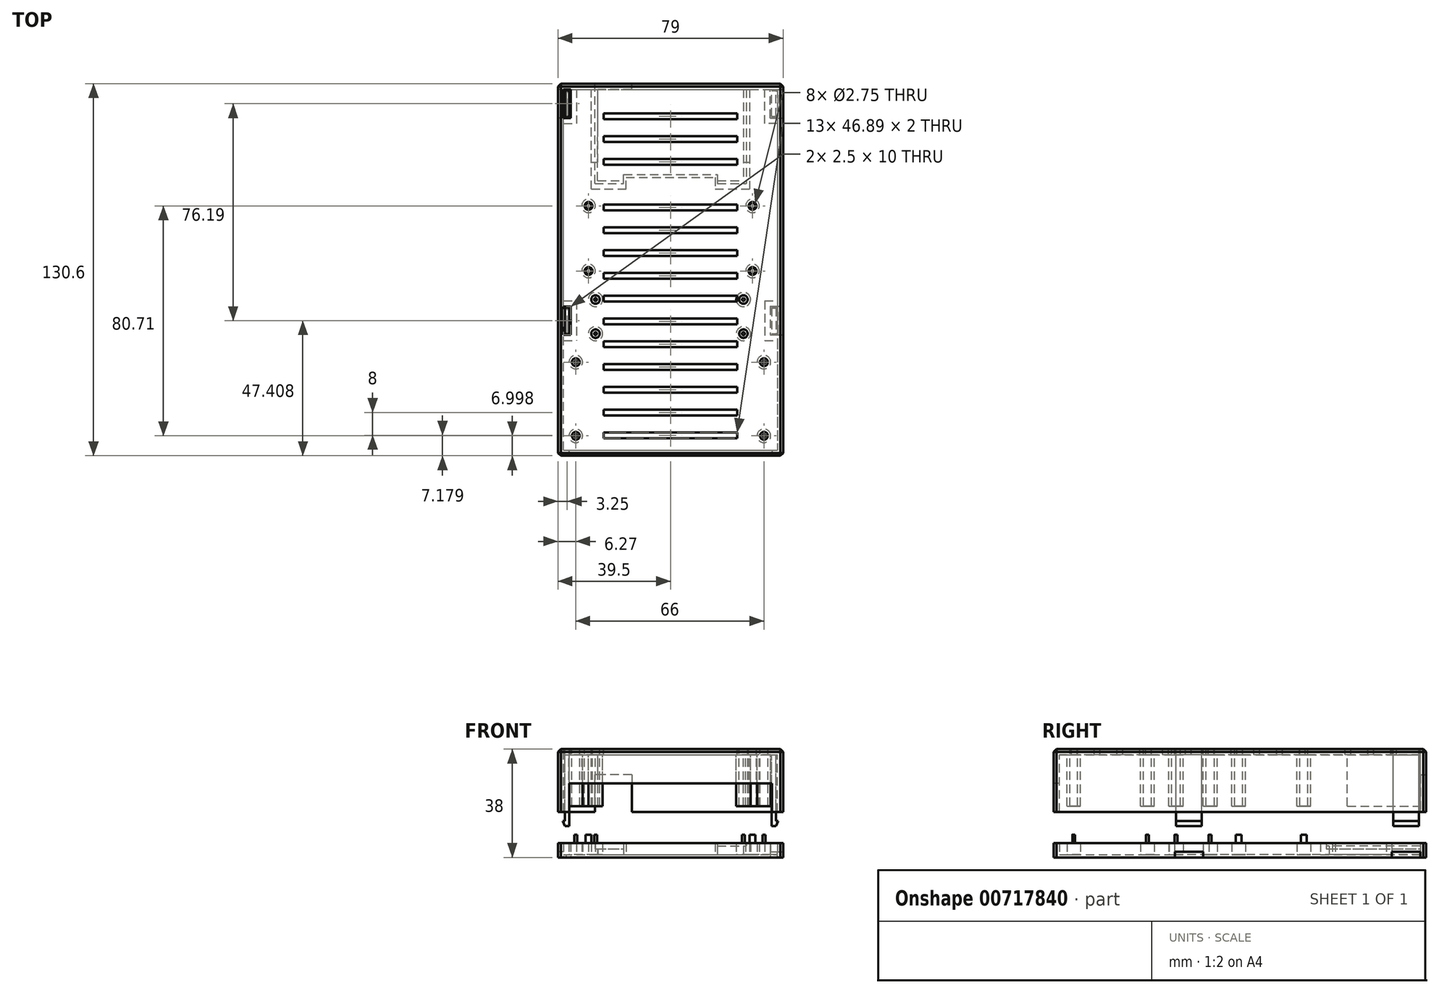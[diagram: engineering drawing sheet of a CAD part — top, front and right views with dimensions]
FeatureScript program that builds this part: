
annotation { "Feature Type Name" : "Feature", "Feature Type Description" : "" }
export const myFeature = defineFeature(function(context is Context, id is Id, definition is map)
    precondition{}
    {
        {
            var Q0;
            Q0=qCreatedBy(makeId("Top.planeOp"),FACE);
            var sketch = newSketch(context, id + "F0", { "sketchPlane" : qUnion([Q0])});
            skLineSegment(sketch, "E0", {"start": v(-75, 58.75) * mm, "end": v(0, 58.75) * mm});
            skLineSegment(sketch, "E1", {"start": v(0, 58.75) * mm, "end": v(0, -67.85) * mm});
            skLineSegment(sketch, "E2", {"start": v(-75, -67.85) * mm, "end": v(-75, 58.75) * mm});
            skCircle(sketch, "E3", {"center": v(-8.73, -5) * mm, "radius": 1 * mm});
            skCircle(sketch, "E4", {"center": v(-66.27, -5) * mm, "radius": 1 * mm});
            skCircle(sketch, "E5", {"center": v(-8.73, 17.86) * mm, "radius": 1 * mm});
            skCircle(sketch, "E6", {"center": v(-66.27, 17.86) * mm, "radius": 1 * mm});
            skLineSegment(sketch, "E7", {"start": v(-75, 17.86) * mm, "end": v(-66.27, 17.86) * mm, "construction": true});
            skLineSegment(sketch, "E8", {"start": v(-8.73, 17.86) * mm, "end": v(0, 17.86) * mm, "construction": true});
            skCircle(sketch, "E9", {"center": v(-66.27, 17.86) * mm, "radius": 2.38 * mm});
            skCircle(sketch, "E10", {"center": v(-66.27, -5) * mm, "radius": 2.38 * mm});
            skCircle(sketch, "E11", {"center": v(-8.73, -5) * mm, "radius": 2.38 * mm});
            skCircle(sketch, "E12", {"center": v(-8.73, 17.86) * mm, "radius": 2.38 * mm});
            skLineSegment(sketch, "E13", {"start": v(-10.95, 58.75) * mm, "end": v(-10.96, 25.75) * mm});
            skLineSegment(sketch, "E14", {"start": v(-64.06, 25.75) * mm, "end": v(-64.05, 58.75) * mm});
            skLineSegment(sketch, "E15", {"start": v(-64.06, 25.75) * mm, "end": v(-53.94, 25.75) * mm});
            skLineSegment(sketch, "E16", {"start": v(-53.94, 25.75) * mm, "end": v(-53.94, 28.86) * mm});
            skLineSegment(sketch, "E17", {"start": v(-53.94, 28.86) * mm, "end": v(-21.08, 28.86) * mm});
            skLineSegment(sketch, "E18", {"start": v(-21.08, 28.86) * mm, "end": v(-21.08, 25.75) * mm});
            skLineSegment(sketch, "E19", {"start": v(-21.08, 25.75) * mm, "end": v(-10.96, 25.75) * mm});
            skLineSegment(sketch, "E20", {"start": v(-75, 47.35) * mm, "end": v(-64.05, 47.35) * mm, "construction": true});
            skLineSegment(sketch, "E21", {"start": v(-10.95, 47.22) * mm, "end": v(0, 47.22) * mm, "construction": true});
            skCircle(sketch, "E22", {"center": v(-11.92, -27) * mm, "radius": 0.5 * mm});
            skCircle(sketch, "E23", {"center": v(-11.92, -15) * mm, "radius": 0.5 * mm});
            skCircle(sketch, "E24", {"center": v(-63.8, -15) * mm, "radius": 0.5 * mm});
            skCircle(sketch, "E25", {"center": v(-63.8, -27) * mm, "radius": 0.5 * mm});
            skCircle(sketch, "E26", {"center": v(-63.8, -27) * mm, "radius": 2.5 * mm});
            skCircle(sketch, "E27", {"center": v(-63.8, -15) * mm, "radius": 2.5 * mm});
            skLineSegment(sketch, "E28.0", {"start": v(-65.26, 23.75) * mm, "end": v(-65.26, 58.75) * mm});
            skLineSegment(sketch, "E28.1", {"start": v(-65.26, 23.75) * mm, "end": v(-53.14, 23.75) * mm});
            skLineSegment(sketch, "E28.3", {"start": v(-53.14, 23.75) * mm, "end": v(-53.14, 27.86) * mm});
            skLineSegment(sketch, "E28.4", {"start": v(-9.74, 58.75) * mm, "end": v(-9.74, 23.75) * mm});
            skLineSegment(sketch, "E28.5", {"start": v(-21.86, 23.75) * mm, "end": v(-9.74, 23.75) * mm});
            skLineSegment(sketch, "E28.6", {"start": v(-21.86, 27.86) * mm, "end": v(-21.86, 23.75) * mm});
            skLineSegment(sketch, "E28.7", {"start": v(-53.14, 27.86) * mm, "end": v(-21.86, 27.86) * mm});
            skLineSegment(sketch, "E29.1", {"start": v(-63.06, 26.75) * mm, "end": v(-53.94, 26.75) * mm});
            skLineSegment(sketch, "E29.2", {"start": v(-63.06, 26.75) * mm, "end": v(-63.05, 58.75) * mm});
            skLineSegment(sketch, "E30.0", {"start": v(-11.95, 58.75) * mm, "end": v(-11.96, 26.75) * mm});
            skLineSegment(sketch, "E30.1", {"start": v(-21.08, 26.75) * mm, "end": v(-11.96, 26.75) * mm});
            skLineSegment(sketch, "E31", {"start": v(-75, -67.85) * mm, "end": v(0, -67.85) * mm});
            skCircle(sketch, "E32", {"center": v(-4.73, -62.85) * mm, "radius": 0.5 * mm});
            skCircle(sketch, "E33", {"center": v(-70.73, -62.85) * mm, "radius": 0.5 * mm});
            skCircle(sketch, "E34", {"center": v(-4.73, -37) * mm, "radius": 0.5 * mm});
            skCircle(sketch, "E35", {"center": v(-70.73, -37) * mm, "radius": 0.5 * mm});
            skCircle(sketch, "E36", {"center": v(-70.73, -37) * mm, "radius": 2.38 * mm});
            skCircle(sketch, "E37", {"center": v(-70.73, -62.85) * mm, "radius": 2.38 * mm});
            skCircle(sketch, "E38", {"center": v(-4.73, -62.85) * mm, "radius": 2.38 * mm});
            skCircle(sketch, "E39", {"center": v(-4.73, -37) * mm, "radius": 2.38 * mm});
            skLineSegment(sketch, "E40", {"start": v(-70.73, -37) * mm, "end": v(-70.73, -27) * mm, "construction": true});
            skLineSegment(sketch, "E41", {"start": v(-4.73, -37) * mm, "end": v(0, -37) * mm, "construction": true});
            skLineSegment(sketch, "E42", {"start": v(-70.73, -37) * mm, "end": v(-75.46, -37) * mm, "construction": true});
            skCircle(sketch, "E43", {"center": v(-11.92, -15) * mm, "radius": 2.5 * mm});
            skCircle(sketch, "E44", {"center": v(-11.92, -27) * mm, "radius": 2.5 * mm});
            skLineSegment(sketch, "E45", {"start": v(-70.73, -62.85) * mm, "end": v(-4.73, -62.85) * mm, "construction": true});
            skLineSegment(sketch, "E46", {"start": v(-4.73, -37) * mm, "end": v(-4.73, -62.85) * mm, "construction": true});
            skLineSegment(sketch, "E47", {"start": v(-66.27, 17.86) * mm, "end": v(-8.73, 17.86) * mm, "construction": true});
            skLineSegment(sketch, "E48", {"start": v(-66.27, 17.86) * mm, "end": v(-66.27, -5) * mm, "construction": true});
            skLineSegment(sketch, "E49", {"start": v(-66.27, -5) * mm, "end": v(-8.73, -5) * mm, "construction": true});
            skLineSegment(sketch, "E50", {"start": v(-8.73, -5) * mm, "end": v(-8.73, 17.86) * mm, "construction": true});
            skLineSegment(sketch, "E51", {"start": v(-70.73, -37) * mm, "end": v(-70.73, -62.85) * mm, "construction": true});
            skLineSegment(sketch, "E52", {"start": v(-70.73, -37) * mm, "end": v(-4.73, -37) * mm, "construction": true});
            skLineSegment(sketch, "E53", {"start": v(-63.8, -15) * mm, "end": v(-11.92, -15) * mm, "construction": true});
            skLineSegment(sketch, "E54", {"start": v(-11.93, -15) * mm, "end": v(-11.93, -27) * mm, "construction": true});
            skLineSegment(sketch, "E55", {"start": v(-11.92, -27) * mm, "end": v(-63.8, -27) * mm, "construction": true});
            skLineSegment(sketch, "E56", {"start": v(-63.8, -27) * mm, "end": v(-63.8, -15) * mm, "construction": true});
            skLineSegment(sketch, "E57", {"start": v(-11.92, -15) * mm, "end": v(0, -15) * mm, "construction": true});
            skLineSegment(sketch, "E58", {"start": v(-63.8, -27) * mm, "end": v(-75, -27) * mm, "construction": true});
            skLineSegment(sketch, "E59", {"start": v(-34.3, -27) * mm, "end": v(-34.3, -37) * mm, "construction": true});
            skLineSegment(sketch, "E60", {"start": v(-45.46, 27.86) * mm, "end": v(-45.46, 17.86) * mm});
            skPoint(sketch, "E61", {"position": v(-37.5, 17.86) * mm});
            skLineSegment(sketch, "E62", {"start": v(-8.73, -5) * mm, "end": v(0, -5) * mm, "construction": true});
            skLineSegment(sketch, "E63", {"start": v(-70.73, -62.85) * mm, "end": v(-70.73, -67.85) * mm, "construction": true});
            skLineSegment(sketch, "E64.0", {"start": v(-77, -69.85) * mm, "end": v(-77, 60.75) * mm});
            skLineSegment(sketch, "E64.1", {"start": v(-77, -69.85) * mm, "end": v(2, -69.85) * mm});
            skLineSegment(sketch, "E64.2", {"start": v(2, 60.75) * mm, "end": v(2, -69.85) * mm});
            skLineSegment(sketch, "E64.3", {"start": v(-77, 60.75) * mm, "end": v(2, 60.75) * mm});
            skLineSegment(sketch, "E65.bottom", {"start": v(-77, -15.44) * mm, "end": v(-70.5, -15.44) * mm});
            skLineSegment(sketch, "E65.top", {"start": v(-77, -29.44) * mm, "end": v(-70.5, -29.44) * mm});
            skLineSegment(sketch, "E65.left", {"start": v(-77, -15.44) * mm, "end": v(-77, -29.44) * mm});
            skLineSegment(sketch, "E65.right", {"start": v(-70.5, -15.44) * mm, "end": v(-70.5, -29.44) * mm});
            skLineSegment(sketch, "E66.0", {"start": v(-75, -17.44) * mm, "end": v(-72.5, -17.44) * mm});
            skLineSegment(sketch, "E66.1", {"start": v(-75, -17.44) * mm, "end": v(-75, -27.44) * mm});
            skLineSegment(sketch, "E66.2", {"start": v(-75, -27.44) * mm, "end": v(-72.5, -27.44) * mm});
            skLineSegment(sketch, "E66.3", {"start": v(-72.5, -17.44) * mm, "end": v(-72.5, -27.44) * mm});
            skLineSegment(sketch, "E67.bottom", {"start": v(-4.5, -15.44) * mm, "end": v(2, -15.44) * mm});
            skLineSegment(sketch, "E67.top", {"start": v(-4.5, -29.44) * mm, "end": v(2, -29.44) * mm});
            skLineSegment(sketch, "E67.left", {"start": v(-4.5, -15.44) * mm, "end": v(-4.5, -29.44) * mm});
            skLineSegment(sketch, "E67.right", {"start": v(2, -15.44) * mm, "end": v(2, -29.44) * mm});
            skLineSegment(sketch, "E68.0", {"start": v(-2.5, -17.44) * mm, "end": v(0, -17.44) * mm});
            skLineSegment(sketch, "E68.1", {"start": v(-2.5, -17.44) * mm, "end": v(-2.5, -27.44) * mm});
            skLineSegment(sketch, "E68.2", {"start": v(-2.5, -27.44) * mm, "end": v(0, -27.44) * mm});
            skLineSegment(sketch, "E68.3", {"start": v(0, -17.44) * mm, "end": v(0, -27.44) * mm});
            skLineSegment(sketch, "E69.bottom", {"start": v(-75, 58.75) * mm, "end": v(-72.5, 58.75) * mm});
            skLineSegment(sketch, "E69.top", {"start": v(-75, 48.75) * mm, "end": v(-72.5, 48.75) * mm});
            skLineSegment(sketch, "E69.left", {"start": v(-75, 58.75) * mm, "end": v(-75, 48.75) * mm});
            skLineSegment(sketch, "E69.right", {"start": v(-72.5, 58.75) * mm, "end": v(-72.5, 48.75) * mm});
            skLineSegment(sketch, "E70", {"start": v(0, 48.75) * mm, "end": v(-2.5, 48.75) * mm});
            skLineSegment(sketch, "E71", {"start": v(-2.5, 48.75) * mm, "end": v(-2.5, 58.75) * mm});
            skLineSegment(sketch, "E72.0", {"start": v(-4.5, 46.75) * mm, "end": v(-4.5, 58.75) * mm});
            skLineSegment(sketch, "E72.1", {"start": v(0, 46.75) * mm, "end": v(-4.5, 46.75) * mm});
            skLineSegment(sketch, "E73.0", {"start": v(-70.5, 58.75) * mm, "end": v(-70.5, 46.75) * mm});
            skLineSegment(sketch, "E73.1", {"start": v(-75, 46.75) * mm, "end": v(-70.5, 46.75) * mm});
            skSolve(sketch);
        }
        {
            var Q0;
            {var subQ10=sQuery(id+"F0.wireOp",EDGE,"E13");Q0=makeQuery(id+"F0.imprint","IMPRINT",FACE,{"disambiguationData":[TD([[makeQuery(id+"F0.imprint","IMPRINT",EDGE,{"derivedFrom":subQ10}),1.0]])]});}
            var Q1;
            Q1=sQuery(id+"F0.wireOp",EDGE,"E15");
            var Q2;
            Q2=sQuery(id+"F0.wireOp",EDGE,"E16");
            var Q3;
            Q3=sQuery(id+"F0.wireOp",EDGE,"E17");
            var Q4;
            Q4=sQuery(id+"F0.wireOp",EDGE,"E28.7");
            var Q5;
            Q5=sQuery(id+"F0.wireOp",EDGE,"E28.3");
            var Q6;
            Q6=sQuery(id+"F0.wireOp",EDGE,"E28.1");
            var Q7;
            Q7=sQuery(id+"F0.wireOp",EDGE,"E28.0");
            var Q8;
            Q8=sQuery(id+"F0.wireOp",EDGE,"E14");
            var Q9;
            Q9=sQuery(id+"F0.wireOp",EDGE,"E28.2");
            var Q10;
            Q10=sQuery(id+"F0.wireOp",EDGE,"XvR5vRtn-6RYL-8VlD-djdF-WygFPbgBNpBE");
            var Q11;
            Q11=sQuery(id+"F0.wireOp",EDGE,"E28.4");
            var Q12;
            Q12=sQuery(id+"F0.wireOp",EDGE,"E13");
            var Q13;
            Q13=sQuery(id+"F0.wireOp",EDGE,"E19");
            var Q14;
            Q14=sQuery(id+"F0.wireOp",EDGE,"E28.5");
            var Q15;
            Q15=sQuery(id+"F0.wireOp",EDGE,"E18");
            var Q16;
            Q16=sQuery(id+"F0.wireOp",EDGE,"E28.6");
            extrude(context, id + "F1", {"entities" : qUnion([Q0]), "surfaceEntities" : qUnion([Q1, Q2, Q3, Q4, Q5, Q6, Q7, Q8, Q9, Q10, Q11, Q12, Q13, Q14, Q15, Q16]), "depth" : 5 * mm, "offsetDistance" : 25 * mm});
        }
        {
            var Q0;
            {var subQ3=sQuery(id+"F0.wireOp",EDGE,"E13");Q0=makeQuery(id+"F0.imprint","IMPRINT",FACE,{"disambiguationData":[TD([[makeQuery(id+"F0.imprint","IMPRINT",EDGE,{"derivedFrom":subQ3}),-1.0]])]});}
            extrude(context, id + "F2", {"entities" : qUnion([Q0]), "operationType" : NewBodyOperationType.ADD, "depth" : 4 * mm, "offsetDistance" : 25 * mm});
        }
        {
            var Q0;
            {var subQ3=sQuery(id+"F0.wireOp",EDGE,"E14");Q0=makeQuery(id+"F0.imprint","IMPRINT",FACE,{"disambiguationData":[TD([[makeQuery(id+"F0.imprint","IMPRINT",EDGE,{"derivedFrom":subQ3}),-1.0]])]});}
            extrude(context, id + "F3", {"entities" : qUnion([Q0]), "operationType" : NewBodyOperationType.ADD, "depth" : 3 * mm, "offsetDistance" : 25 * mm});
        }
        {
            var Q0;
            {var subQ1=sQuery(id+"F0.wireOp",EDGE,"Yi5yYVMC-fJF2-kBoP-Mys3-r5TxYGe0o32l");Q0=makeQuery(id+"F0.imprint","IMPRINT",FACE,{"disambiguationData":[TD([[makeQuery(id+"F0.imprint","IMPRINT",EDGE,{"derivedFrom":subQ1}),-1.0]])]});}
            var Q1;
            {var subQ4=sQuery(id+"F0.wireOp",EDGE,"Yi5yYVMC-fJF2-kBoP-Mys3-r5TxYGe0o32l");Q1=makeQuery(id+"F0.imprint","IMPRINT",FACE,{"disambiguationData":[TD([[makeQuery(id+"F0.imprint","IMPRINT",EDGE,{"derivedFrom":subQ4}),1.0]])]});}
            var Q2;
            {var subQ1=sQuery(id+"F0.wireOp",EDGE,"0YCsy9lb-VRbT-LKH3-aLzf-e1dkMKbICIHK");Q2=makeQuery(id+"F0.imprint","IMPRINT",FACE,{"disambiguationData":[TD([[makeQuery(id+"F0.imprint","IMPRINT",EDGE,{"derivedFrom":subQ1}),-1.0]])]});}
            var Q3;
            Q3=makeQuery(id+"F0.imprint","IMPRINT",FACE,{"disambiguationData":[TD([[makeQuery(id+"F0.imprint","IMPRINT",EDGE,{"derivedFrom":sQuery(id+"F0.wireOp",EDGE,"0YCsy9lb-VRbT-LKH3-aLzf-e1dkMKbICIHK")}),1.0]])]});
            var Q4;
            {var subQ3=sQuery(id+"F0.wireOp",EDGE,"8QSHRwWJ-kWPb-99zj-fMYM-cOQBIvpf0yN0");Q4=makeQuery(id+"F0.imprint","IMPRINT",FACE,{"disambiguationData":[TD([[makeQuery(id+"F0.imprint","IMPRINT",EDGE,{"derivedFrom":subQ3}),-1.0]])]});}
            var Q5;
            {var subQ0=sQuery(id+"F0.wireOp",EDGE,"E0");Q5=makeQuery(id+"F0.imprint","IMPRINT",FACE,{"disambiguationData":[TD([[makeQuery(id+"F0.imprint","IMPRINT",EDGE,{"derivedFrom":subQ0}),-1.0]])]});}
            var Q6;
            {var subQ4=sQuery(id+"F0.wireOp",EDGE,"E1");Q6=makeQuery(id+"F0.imprint","IMPRINT",FACE,{"disambiguationData":[TD([[makeQuery(id+"F0.imprint","IMPRINT",EDGE,{"derivedFrom":subQ4}),-1.0]])]});}
            var Q7;
            Q7=makeQuery(id+"F0.imprint","IMPRINT",FACE,{"disambiguationData":[TD([[makeQuery(id+"F0.imprint","IMPRINT",EDGE,{"derivedFrom":sQuery(id+"F0.wireOp",EDGE,"E9")}),-1.0]])]});
            extrude(context, id + "F4", {"entities" : qUnion([Q0, Q1, Q2, Q3, Q4, Q5, Q6, Q7]), "operationType" : NewBodyOperationType.ADD, "depth" : 1 * mm, "offsetDistance" : 25 * mm});
        }
        {
            var Q0;
            Q0=makeQuery(id+"F0.imprint","IMPRINT",FACE,{"disambiguationData":[TD([[makeQuery(id+"F0.imprint","IMPRINT",EDGE,{"derivedFrom":sQuery(id+"F0.wireOp",EDGE,"E6")}),-1.0]])]});
            var Q1;
            Q1=makeQuery(id+"F0.imprint","IMPRINT",FACE,{"disambiguationData":[TD([[makeQuery(id+"F0.imprint","IMPRINT",EDGE,{"derivedFrom":sQuery(id+"F0.wireOp",EDGE,"E5")}),-1.0]])]});
            var Q2;
            Q2=makeQuery(id+"F0.imprint","IMPRINT",FACE,{"disambiguationData":[TD([[makeQuery(id+"F0.imprint","IMPRINT",EDGE,{"derivedFrom":sQuery(id+"F0.wireOp",EDGE,"E3")}),-1.0]])]});
            var Q3;
            Q3=makeQuery(id+"F0.imprint","IMPRINT",FACE,{"disambiguationData":[TD([[makeQuery(id+"F0.imprint","IMPRINT",EDGE,{"derivedFrom":sQuery(id+"F0.wireOp",EDGE,"E25")}),-1.0]])]});
            var Q4;
            Q4=makeQuery(id+"F0.imprint","IMPRINT",FACE,{"disambiguationData":[TD([[makeQuery(id+"F0.imprint","IMPRINT",EDGE,{"derivedFrom":sQuery(id+"F0.wireOp",EDGE,"E24")}),-1.0]])]});
            var Q5;
            Q5=makeQuery(id+"F0.imprint","IMPRINT",FACE,{"disambiguationData":[TD([[makeQuery(id+"F0.imprint","IMPRINT",EDGE,{"derivedFrom":sQuery(id+"F0.wireOp",EDGE,"E4")}),-1.0]])]});
            var Q6;
            Q6=makeQuery(id+"F0.imprint","IMPRINT",FACE,{"disambiguationData":[TD([[makeQuery(id+"F0.imprint","IMPRINT",EDGE,{"derivedFrom":sQuery(id+"F0.wireOp",EDGE,"E23")}),-1.0]])]});
            var Q7;
            Q7=makeQuery(id+"F0.imprint","IMPRINT",FACE,{"disambiguationData":[TD([[makeQuery(id+"F0.imprint","IMPRINT",EDGE,{"derivedFrom":sQuery(id+"F0.wireOp",EDGE,"E22")}),-1.0]])]});
            var Q8;
            Q8=makeQuery(id+"F0.imprint","IMPRINT",FACE,{"disambiguationData":[TD([[makeQuery(id+"F0.imprint","IMPRINT",EDGE,{"derivedFrom":sQuery(id+"F0.wireOp",EDGE,"E35")}),-1.0]])]});
            var Q9;
            Q9=makeQuery(id+"F0.imprint","IMPRINT",FACE,{"disambiguationData":[TD([[makeQuery(id+"F0.imprint","IMPRINT",EDGE,{"derivedFrom":sQuery(id+"F0.wireOp",EDGE,"E34")}),-1.0]])]});
            var Q10;
            Q10=makeQuery(id+"F0.imprint","IMPRINT",FACE,{"disambiguationData":[TD([[makeQuery(id+"F0.imprint","IMPRINT",EDGE,{"derivedFrom":sQuery(id+"F0.wireOp",EDGE,"E32")}),-1.0]])]});
            var Q11;
            Q11=makeQuery(id+"F0.imprint","IMPRINT",FACE,{"disambiguationData":[TD([[makeQuery(id+"F0.imprint","IMPRINT",EDGE,{"derivedFrom":sQuery(id+"F0.wireOp",EDGE,"E33")}),-1.0]])]});
            extrude(context, id + "F5", {"entities" : qUnion([Q0, Q1, Q2, Q3, Q4, Q5, Q6, Q7, Q8, Q9, Q10, Q11]), "operationType" : NewBodyOperationType.ADD, "depth" : 5 * mm, "offsetDistance" : 25 * mm});
        }
        {
            var Q0;
            {var subQ1=sQuery(id+"F0.wireOp",EDGE,"E17");Q0=makeQuery(id+"F0.imprint","IMPRINT",FACE,{"disambiguationData":[TD([[makeQuery(id+"F0.imprint","IMPRINT",EDGE,{"derivedFrom":subQ1}),1.0]])]});}
            extrude(context, id + "F6", {"entities" : qUnion([Q0]), "operationType" : NewBodyOperationType.ADD, "depth" : 1 * mm, "offsetDistance" : 25 * mm});
        }
        {
            var Q0;
            Q0=makeQuery(id+"F0.imprint","IMPRINT",FACE,{"disambiguationData":[TD([[makeQuery(id+"F0.imprint","IMPRINT",EDGE,{"derivedFrom":sQuery(id+"F0.wireOp",EDGE,"E6")}),1.0]])]});
            var Q1;
            Q1=makeQuery(id+"F0.imprint","IMPRINT",FACE,{"disambiguationData":[TD([[makeQuery(id+"F0.imprint","IMPRINT",EDGE,{"derivedFrom":sQuery(id+"F0.wireOp",EDGE,"E5")}),1.0]])]});
            var Q2;
            Q2=makeQuery(id+"F0.imprint","IMPRINT",FACE,{"disambiguationData":[TD([[makeQuery(id+"F0.imprint","IMPRINT",EDGE,{"derivedFrom":sQuery(id+"F0.wireOp",EDGE,"E3")}),1.0]])]});
            var Q3;
            Q3=makeQuery(id+"F0.imprint","IMPRINT",FACE,{"disambiguationData":[TD([[makeQuery(id+"F0.imprint","IMPRINT",EDGE,{"derivedFrom":sQuery(id+"F0.wireOp",EDGE,"E4")}),1.0]])]});
            var Q4;
            Q4=makeQuery(id+"F0.imprint","IMPRINT",FACE,{"disambiguationData":[TD([[makeQuery(id+"F0.imprint","IMPRINT",EDGE,{"derivedFrom":sQuery(id+"F0.wireOp",EDGE,"E24")}),1.0]])]});
            var Q5;
            Q5=makeQuery(id+"F0.imprint","IMPRINT",FACE,{"disambiguationData":[TD([[makeQuery(id+"F0.imprint","IMPRINT",EDGE,{"derivedFrom":sQuery(id+"F0.wireOp",EDGE,"E23")}),1.0]])]});
            var Q6;
            Q6=makeQuery(id+"F0.imprint","IMPRINT",FACE,{"disambiguationData":[TD([[makeQuery(id+"F0.imprint","IMPRINT",EDGE,{"derivedFrom":sQuery(id+"F0.wireOp",EDGE,"E22")}),1.0]])]});
            var Q7;
            Q7=makeQuery(id+"F0.imprint","IMPRINT",FACE,{"disambiguationData":[TD([[makeQuery(id+"F0.imprint","IMPRINT",EDGE,{"derivedFrom":sQuery(id+"F0.wireOp",EDGE,"E25")}),1.0]])]});
            var Q8;
            Q8=makeQuery(id+"F0.imprint","IMPRINT",FACE,{"disambiguationData":[TD([[makeQuery(id+"F0.imprint","IMPRINT",EDGE,{"derivedFrom":sQuery(id+"F0.wireOp",EDGE,"E35")}),1.0]])]});
            var Q9;
            Q9=makeQuery(id+"F0.imprint","IMPRINT",FACE,{"disambiguationData":[TD([[makeQuery(id+"F0.imprint","IMPRINT",EDGE,{"derivedFrom":sQuery(id+"F0.wireOp",EDGE,"E33")}),1.0]])]});
            var Q10;
            Q10=makeQuery(id+"F0.imprint","IMPRINT",FACE,{"disambiguationData":[TD([[makeQuery(id+"F0.imprint","IMPRINT",EDGE,{"derivedFrom":sQuery(id+"F0.wireOp",EDGE,"E34")}),1.0]])]});
            var Q11;
            Q11=makeQuery(id+"F0.imprint","IMPRINT",FACE,{"disambiguationData":[TD([[makeQuery(id+"F0.imprint","IMPRINT",EDGE,{"derivedFrom":sQuery(id+"F0.wireOp",EDGE,"E32")}),1.0]])]});
            extrude(context, id + "F7", {"entities" : qUnion([Q0, Q1, Q2, Q3, Q4, Q5, Q6, Q7, Q8, Q9, Q10, Q11]), "operationType" : NewBodyOperationType.ADD, "depth" : 8 * mm, "offsetDistance" : 25 * mm});
        }
        {
            var Q0;
            {var subQ0=sQuery(id+"F0.wireOp",EDGE,"E65.right");Q0=makeQuery(id+"F0.imprint","IMPRINT",FACE,{"disambiguationData":[TD([[makeQuery(id+"F0.imprint","IMPRINT",EDGE,{"derivedFrom":subQ0}),-1.0]])]});}
            var Q1;
            {var subQ0=sQuery(id+"F0.wireOp",EDGE,"E67.left");Q1=makeQuery(id+"F0.imprint","IMPRINT",FACE,{"disambiguationData":[TD([[makeQuery(id+"F0.imprint","IMPRINT",EDGE,{"derivedFrom":subQ0}),1.0]])]});}
            var Q2;
            {var subQ0=sQuery(id+"F0.wireOp",EDGE,"YggwEhy4-TLBy-cti2-uv1J-cCnbuqqM2Ind");Q2=makeQuery(id+"F0.imprint","IMPRINT",FACE,{"disambiguationData":[TD([[makeQuery(id+"F0.imprint","IMPRINT",EDGE,{"derivedFrom":subQ0}),-1.0]])]});}
            var Q3;
            {var subQ0=sQuery(id+"F0.wireOp",EDGE,"Ja4ARaNF-FQ16-Zxaf-2BLZ-pRakPvsBmFni.top");Q3=makeQuery(id+"F0.imprint","IMPRINT",FACE,{"disambiguationData":[TD([[makeQuery(id+"F0.imprint","IMPRINT",EDGE,{"derivedFrom":subQ0}),-1.0]])]});}
            var Q4;
            {var subQ1=sQuery(id+"F0.wireOp",EDGE,"E69.top");Q4=makeQuery(id+"F0.imprint","IMPRINT",FACE,{"disambiguationData":[TD([[makeQuery(id+"F0.imprint","IMPRINT",EDGE,{"derivedFrom":subQ1}),-1.0]])]});}
            var Q5;
            {var subQ0=sQuery(id+"F0.wireOp",EDGE,"E70");Q5=makeQuery(id+"F0.imprint","IMPRINT",FACE,{"disambiguationData":[TD([[makeQuery(id+"F0.imprint","IMPRINT",EDGE,{"derivedFrom":subQ0}),1.0]])]});}
            extrude(context, id + "F8", {"entities" : qUnion([Q0, Q1, Q2, Q3, Q4, Q5]), "operationType" : NewBodyOperationType.ADD, "depth" : 5 * mm, "offsetDistance" : 25 * mm});
        }
        {
            var Q0;
            Q0 = qSketchRegion(id + "F0", true);
            extrude(context, id + "F9", {"entities" : qUnion([Q0]), "operationType" : NewBodyOperationType.ADD, "depth" : 5 * mm, "offsetDistance" : 25 * mm});
        }
        {
            var Q0;
            Q0=makeQuery(id+"F4.opExtrude","CAP_FACE",FACE,{"disambiguationData":[OSD([sQuery(id+"F0.wireOp",EDGE,"E0"),sQuery(id+"F0.wireOp",EDGE,"E1"),sQuery(id+"F0.wireOp",EDGE,"E2"),sQuery(id+"F0.wireOp",EDGE,"E9"),sQuery(id+"F0.wireOp",EDGE,"E10"),sQuery(id+"F0.wireOp",EDGE,"E11"),sQuery(id+"F0.wireOp",EDGE,"E12"),sQuery(id+"F0.wireOp",EDGE,"E26"),sQuery(id+"F0.wireOp",EDGE,"E27"),sQuery(id+"F0.wireOp",EDGE,"E28.0"),sQuery(id+"F0.wireOp",EDGE,"E28.1"),sQuery(id+"F0.wireOp",EDGE,"E28.3"),sQuery(id+"F0.wireOp",EDGE,"E28.4"),sQuery(id+"F0.wireOp",EDGE,"E28.5"),sQuery(id+"F0.wireOp",EDGE,"E28.6"),sQuery(id+"F0.wireOp",EDGE,"E28.7"),sQuery(id+"F0.wireOp",EDGE,"E31"),sQuery(id+"F0.wireOp",EDGE,"E36"),sQuery(id+"F0.wireOp",EDGE,"E37"),sQuery(id+"F0.wireOp",EDGE,"E38"),sQuery(id+"F0.wireOp",EDGE,"E39"),sQuery(id+"F0.wireOp",EDGE,"E43"),sQuery(id+"F0.wireOp",EDGE,"E44"),sQuery(id+"F0.wireOp",EDGE,"E65.bottom"),sQuery(id+"F0.wireOp",EDGE,"E65.top"),sQuery(id+"F0.wireOp",EDGE,"E65.right"),sQuery(id+"F0.wireOp",EDGE,"E68.0"),sQuery(id+"F0.wireOp",EDGE,"E68.1"),sQuery(id+"F0.wireOp",EDGE,"E68.2"),sQuery(id+"F0.wireOp",EDGE,"E72.0"),sQuery(id+"F0.wireOp",EDGE,"E72.1"),sQuery(id+"F0.wireOp",EDGE,"E73.0"),sQuery(id+"F0.wireOp",EDGE,"E73.1")])],"isStart":false});
            cPlane(context, id + "F10", {"entities" : qUnion([Q0]), "cplaneType" : CPlaneType.OFFSET, "offset" : 37 * mm, "width" : 150 * mm, "height" : 150 * mm});
        }
        {
            var Q0;
            Q0=qCreatedBy(id+"F10.planeOp",FACE);
            var sketch = newSketch(context, id + "F11", { "sketchPlane" : qUnion([Q0])});
            skLineSegment(sketch, "E74", {"start": v(-65.26, 33.14) * mm, "end": v(-63.05, 33.14) * mm});
            skLineSegment(sketch, "E75", {"start": v(-63.05, 33.14) * mm, "end": v(-11.95, 33.14) * mm, "construction": true});
            skLineSegment(sketch, "E76", {"start": v(-11.95, 33.14) * mm, "end": v(-9.74, 33.14) * mm});
            skCircle(sketch, "E77.0", {"center": v(-66.27, 17.86) * mm, "radius": 2.38 * mm});
            skCircle(sketch, "E78.0", {"center": v(-8.73, 17.86) * mm, "radius": 2.38 * mm});
            skPoint(sketch, "E78.1", {"position": v(-8.73, 17.86) * mm});
            skCircle(sketch, "E79.0", {"center": v(-66.27, -5) * mm, "radius": 2.38 * mm});
            skPoint(sketch, "E79.1", {"position": v(-66.27, -5) * mm});
            skCircle(sketch, "E80.0", {"center": v(-8.73, -5) * mm, "radius": 2.38 * mm});
            skPoint(sketch, "E80.1", {"position": v(-8.73, -5) * mm});
            skCircle(sketch, "E81.0", {"center": v(-63.8, -15) * mm, "radius": 2.5 * mm});
            skPoint(sketch, "E81.1", {"position": v(-63.8, -15) * mm});
            skPoint(sketch, "E81.2", {"position": v(-11.92, -15) * mm});
            skCircle(sketch, "E81.3", {"center": v(-11.92, -15) * mm, "radius": 2.5 * mm});
            skCircle(sketch, "E81.4", {"center": v(-11.92, -27) * mm, "radius": 2.5 * mm});
            skPoint(sketch, "E81.5", {"position": v(-11.92, -27) * mm});
            skCircle(sketch, "E81.6", {"center": v(-63.8, -27) * mm, "radius": 2.5 * mm});
            skPoint(sketch, "E81.7", {"position": v(-63.8, -27) * mm});
            skCircle(sketch, "E81.8", {"center": v(-70.73, -37) * mm, "radius": 2.38 * mm});
            skPoint(sketch, "E81.9", {"position": v(-70.73, -37) * mm});
            skCircle(sketch, "E81.10", {"center": v(-4.73, -37) * mm, "radius": 2.38 * mm});
            skPoint(sketch, "E81.11", {"position": v(-4.73, -37) * mm});
            skCircle(sketch, "E81.12", {"center": v(-70.73, -62.85) * mm, "radius": 2.38 * mm});
            skPoint(sketch, "E81.13", {"position": v(-70.73, -62.85) * mm});
            skCircle(sketch, "E81.14", {"center": v(-4.73, -62.85) * mm, "radius": 2.38 * mm});
            skPoint(sketch, "E81.15", {"position": v(-4.73, -62.85) * mm});
            skLineSegment(sketch, "E82.0", {"start": v(-75, 58.75) * mm, "end": v(0, 58.75) * mm});
            skLineSegment(sketch, "E83.0", {"start": v(-75, -67.85) * mm, "end": v(-75, 58.75) * mm});
            skLineSegment(sketch, "E84.0", {"start": v(-77, -69.85) * mm, "end": v(-77, 60.75) * mm});
            skLineSegment(sketch, "E85.0", {"start": v(-77, -69.85) * mm, "end": v(2, -69.85) * mm});
            skLineSegment(sketch, "E86.0", {"start": v(2, 60.75) * mm, "end": v(2, -69.85) * mm});
            skLineSegment(sketch, "E87.0", {"start": v(-77, 60.75) * mm, "end": v(2, 60.75) * mm});
            skLineSegment(sketch, "E88.0", {"start": v(-75, -67.85) * mm, "end": v(0, -67.85) * mm});
            skLineSegment(sketch, "E89.0", {"start": v(0, 58.75) * mm, "end": v(0, -67.85) * mm});
            skLineSegment(sketch, "E90.0", {"start": v(-2.5, 48.75) * mm, "end": v(-2.5, 58.75) * mm});
            skLineSegment(sketch, "E90.1", {"start": v(0, 48.75) * mm, "end": v(-2.5, 48.75) * mm});
            skLineSegment(sketch, "E91.0", {"start": v(-2.5, -17.44) * mm, "end": v(-2.5, -27.44) * mm});
            skLineSegment(sketch, "E92.0", {"start": v(-2.5, -27.44) * mm, "end": v(0, -27.44) * mm});
            skLineSegment(sketch, "E93.0", {"start": v(-2.5, -17.44) * mm, "end": v(0, -17.44) * mm});
            skLineSegment(sketch, "E94.0", {"start": v(0, -17.44) * mm, "end": v(0, -27.44) * mm});
            skLineSegment(sketch, "E95.0", {"start": v(-75, -27.44) * mm, "end": v(-75, -17.44) * mm});
            skLineSegment(sketch, "E96.0", {"start": v(-75, -17.44) * mm, "end": v(-72.5, -17.44) * mm});
            skLineSegment(sketch, "E97.0", {"start": v(-72.5, -17.44) * mm, "end": v(-72.5, -27.44) * mm});
            skLineSegment(sketch, "E98.0", {"start": v(-75, -27.44) * mm, "end": v(-72.5, -27.44) * mm});
            skLineSegment(sketch, "E99.0", {"start": v(-74.5, -26.94) * mm, "end": v(-74.5, -17.94) * mm});
            skLineSegment(sketch, "E99.1", {"start": v(-74.5, -26.94) * mm, "end": v(-73, -26.94) * mm});
            skLineSegment(sketch, "E99.2", {"start": v(-73, -17.94) * mm, "end": v(-73, -26.94) * mm});
            skLineSegment(sketch, "E99.3", {"start": v(-74.5, -17.94) * mm, "end": v(-73, -17.94) * mm});
            skLineSegment(sketch, "E100.0", {"start": v(-2, -17.94) * mm, "end": v(-0.5, -17.94) * mm});
            skLineSegment(sketch, "E100.1", {"start": v(-2, -17.94) * mm, "end": v(-2, -26.94) * mm});
            skLineSegment(sketch, "E100.2", {"start": v(-2, -26.94) * mm, "end": v(-0.5, -26.94) * mm});
            skLineSegment(sketch, "E100.3", {"start": v(-0.5, -17.94) * mm, "end": v(-0.5, -26.94) * mm});
            skLineSegment(sketch, "E101", {"start": v(0, 48.75) * mm, "end": v(0, 58.75) * mm});
            skLineSegment(sketch, "E102", {"start": v(0, 58.75) * mm, "end": v(-2.5, 58.75) * mm});
            skLineSegment(sketch, "E103.0", {"start": v(-0.5, 49.25) * mm, "end": v(-0.5, 58.25) * mm});
            skLineSegment(sketch, "E103.1", {"start": v(-0.5, 49.25) * mm, "end": v(-2, 49.25) * mm});
            skLineSegment(sketch, "E103.2", {"start": v(-2, 49.25) * mm, "end": v(-2, 58.25) * mm});
            skLineSegment(sketch, "E103.3", {"start": v(-0.5, 58.25) * mm, "end": v(-2, 58.25) * mm});
            skLineSegment(sketch, "E104.0", {"start": v(-75, 48.75) * mm, "end": v(-75, 58.75) * mm});
            skLineSegment(sketch, "E105.0", {"start": v(-75, 48.75) * mm, "end": v(-72.5, 48.75) * mm});
            skLineSegment(sketch, "E106.0", {"start": v(-72.5, 58.75) * mm, "end": v(-72.5, 48.75) * mm});
            skLineSegment(sketch, "E107.0", {"start": v(-75, 58.75) * mm, "end": v(-72.5, 58.75) * mm});
            skLineSegment(sketch, "E108", {"start": v(-72.5, 58.75) * mm, "end": v(-75, 58.75) * mm});
            skLineSegment(sketch, "E109.0", {"start": v(-73, 58.25) * mm, "end": v(-74.5, 58.25) * mm});
            skLineSegment(sketch, "E109.1", {"start": v(-73, 58.25) * mm, "end": v(-73, 49.25) * mm});
            skLineSegment(sketch, "E109.2", {"start": v(-74.5, 49.25) * mm, "end": v(-73, 49.25) * mm});
            skLineSegment(sketch, "E109.3", {"start": v(-74.5, 49.25) * mm, "end": v(-74.5, 58.25) * mm});
            skLineSegment(sketch, "E110.0", {"start": v(-65.26, 23.75) * mm, "end": v(-65.26, 58.75) * mm});
            skLineSegment(sketch, "E111.0", {"start": v(-63.06, 26.75) * mm, "end": v(-63.05, 58.75) * mm});
            skLineSegment(sketch, "E112.0", {"start": v(-9.74, 58.75) * mm, "end": v(-9.74, 23.75) * mm});
            skLineSegment(sketch, "E113.0", {"start": v(-11.95, 58.75) * mm, "end": v(-11.96, 26.75) * mm});
            skLineSegment(sketch, "E114", {"start": v(-11.96, 26.75) * mm, "end": v(-9.74, 23.75) * mm});
            skLineSegment(sketch, "E115", {"start": v(-63.06, 26.75) * mm, "end": v(-65.26, 23.75) * mm});
            skCircle(sketch, "E116.0", {"center": v(-66.27, 17.86) * mm, "radius": 1.38 * mm});
            skCircle(sketch, "E117.0", {"center": v(-66.27, -5) * mm, "radius": 1.38 * mm});
            skCircle(sketch, "E118.0", {"center": v(-63.8, -15) * mm, "radius": 1.5 * mm});
            skCircle(sketch, "E119.0", {"center": v(-63.8, -27) * mm, "radius": 1.5 * mm});
            skCircle(sketch, "E120.0", {"center": v(-70.73, -37) * mm, "radius": 1.38 * mm});
            skCircle(sketch, "E121.0", {"center": v(-70.73, -62.85) * mm, "radius": 1.38 * mm});
            skCircle(sketch, "E122.0", {"center": v(-4.73, -62.85) * mm, "radius": 1.38 * mm});
            skCircle(sketch, "E123.0", {"center": v(-4.73, -37) * mm, "radius": 1.38 * mm});
            skCircle(sketch, "E124.0", {"center": v(-11.92, -27) * mm, "radius": 1.5 * mm});
            skCircle(sketch, "E125.0", {"center": v(-11.92, -15) * mm, "radius": 1.5 * mm});
            skCircle(sketch, "E126.0", {"center": v(-8.73, -5) * mm, "radius": 1.38 * mm});
            skCircle(sketch, "E127.0", {"center": v(-8.73, 17.86) * mm, "radius": 1.38 * mm});
            skSolve(sketch);
        }
        {
            var Q0;
            Q0=makeQuery(id+"F11.imprint","IMPRINT",FACE,{"disambiguationData":[TD([[makeQuery(id+"F11.imprint","IMPRINT",EDGE,{"derivedFrom":sQuery(id+"F11.wireOp",EDGE,"e2144d62-b7ac-4b5f-b738-c244b41c5520.0")}),-1.0]])]});
            var Q1;
            Q1=makeQuery(id+"F11.imprint","IMPRINT",FACE,{"disambiguationData":[TD([[makeQuery(id+"F11.imprint","IMPRINT",EDGE,{"derivedFrom":sQuery(id+"F11.wireOp",EDGE,"E82.0")}),1.0]])]});
            extrude(context, id + "F12", {"entities" : qUnion([Q0, Q1]), "operationType" : NewBodyOperationType.ADD, "depth" : -22 * mm, "offsetDistance" : 25 * mm});
        }
        {
            var Q0;
            {var subQ0=sQuery(id+"F11.wireOp",EDGE,"E74");Q0=makeQuery(id+"F11.imprint","IMPRINT",FACE,{"disambiguationData":[TD([[makeQuery(id+"F11.imprint","IMPRINT",EDGE,{"derivedFrom":subQ0}),1.0]])]});}
            var Q1;
            {var subQ0=sQuery(id+"F11.wireOp",EDGE,"E76");Q1=makeQuery(id+"F11.imprint","IMPRINT",FACE,{"disambiguationData":[TD([[makeQuery(id+"F11.imprint","IMPRINT",EDGE,{"derivedFrom":subQ0}),1.0]])]});}
            extrude(context, id + "F13", {"entities" : qUnion([Q0, Q1]), "operationType" : NewBodyOperationType.ADD, "depth" : -20 * mm, "offsetDistance" : 25 * mm});
        }
        {
            var Q0;
            Q0=makeQuery(id+"F11.imprint","IMPRINT",FACE,{"disambiguationData":[TD([[makeQuery(id+"F11.imprint","IMPRINT",EDGE,{"derivedFrom":sQuery(id+"F11.wireOp",EDGE,"26c1f2c4-f0f0-4c1f-a497-fe7e13373d30.0")}),-1.0]])]});
            var Q1;
            Q1=makeQuery(id+"F11.imprint","IMPRINT",FACE,{"disambiguationData":[TD([[makeQuery(id+"F11.imprint","IMPRINT",EDGE,{"derivedFrom":sQuery(id+"F11.wireOp",EDGE,"E77.0")}),-1.0]])]});
            var Q2;
            Q2=makeQuery(id+"F11.imprint","IMPRINT",FACE,{"disambiguationData":[TD([[makeQuery(id+"F11.imprint","IMPRINT",EDGE,{"derivedFrom":sQuery(id+"F11.wireOp",EDGE,"E95.0")}),-1.0]])]});
            var Q3;
            Q3=makeQuery(id+"F11.imprint","IMPRINT",FACE,{"disambiguationData":[TD([[makeQuery(id+"F11.imprint","IMPRINT",EDGE,{"derivedFrom":sQuery(id+"F11.wireOp",EDGE,"E104.0")}),-1.0]])]});
            var Q4;
            Q4=makeQuery(id+"F11.imprint","IMPRINT",FACE,{"disambiguationData":[TD([[makeQuery(id+"F11.imprint","IMPRINT",EDGE,{"derivedFrom":sQuery(id+"F11.wireOp",EDGE,"E90.0")}),-1.0]])]});
            var Q5;
            Q5=makeQuery(id+"F11.imprint","IMPRINT",FACE,{"disambiguationData":[TD([[makeQuery(id+"F11.imprint","IMPRINT",EDGE,{"derivedFrom":sQuery(id+"F11.wireOp",EDGE,"E91.0")}),1.0]])]});
            var Q6;
            {var subQ0=sQuery(id+"F11.wireOp",EDGE,"E76");Q6=makeQuery(id+"F11.imprint","IMPRINT",FACE,{"disambiguationData":[TD([[makeQuery(id+"F11.imprint","IMPRINT",EDGE,{"derivedFrom":subQ0}),-1.0]])]});}
            var Q7;
            {var subQ0=sQuery(id+"F11.wireOp",EDGE,"E74");Q7=makeQuery(id+"F11.imprint","IMPRINT",FACE,{"disambiguationData":[TD([[makeQuery(id+"F11.imprint","IMPRINT",EDGE,{"derivedFrom":subQ0}),-1.0]])]});}
            extrude(context, id + "F14", {"entities" : qUnion([Q0, Q1, Q2, Q3, Q4, Q5, Q6, Q7]), "operationType" : NewBodyOperationType.ADD, "depth" : -2 * mm, "offsetDistance" : 25 * mm});
        }
        {
            var Q0;
            Q0=makeQuery(id+"F11.imprint","IMPRINT",FACE,{"disambiguationData":[TD([[makeQuery(id+"F11.imprint","IMPRINT",EDGE,{"derivedFrom":sQuery(id+"F11.wireOp",EDGE,"E109.0")}),1.0]])]});
            var Q1;
            Q1=makeQuery(id+"F11.imprint","IMPRINT",FACE,{"disambiguationData":[TD([[makeQuery(id+"F11.imprint","IMPRINT",EDGE,{"derivedFrom":sQuery(id+"F11.wireOp",EDGE,"E103.0")}),1.0]])]});
            var Q2;
            Q2=makeQuery(id+"F11.imprint","IMPRINT",FACE,{"disambiguationData":[TD([[makeQuery(id+"F11.imprint","IMPRINT",EDGE,{"derivedFrom":sQuery(id+"F11.wireOp",EDGE,"E99.0")}),-1.0]])]});
            var Q3;
            Q3=makeQuery(id+"F11.imprint","IMPRINT",FACE,{"disambiguationData":[TD([[makeQuery(id+"F11.imprint","IMPRINT",EDGE,{"derivedFrom":sQuery(id+"F11.wireOp",EDGE,"E100.0")}),-1.0]])]});
            extrude(context, id + "F15", {"entities" : qUnion([Q0, Q1, Q2, Q3]), "operationType" : NewBodyOperationType.ADD, "depth" : -27 * mm, "offsetDistance" : 25 * mm});
        }
        {
            var Q0;
            Q0=makeQuery(id+"F11.imprint","IMPRINT",FACE,{"disambiguationData":[TD([[makeQuery(id+"F11.imprint","IMPRINT",EDGE,{"derivedFrom":sQuery(id+"F11.wireOp",EDGE,"E77.0")}),1.0]])]});
            var Q1;
            Q1=makeQuery(id+"F11.imprint","IMPRINT",FACE,{"disambiguationData":[TD([[makeQuery(id+"F11.imprint","IMPRINT",EDGE,{"derivedFrom":sQuery(id+"F11.wireOp",EDGE,"E78.0")}),1.0]])]});
            var Q2;
            Q2=makeQuery(id+"F11.imprint","IMPRINT",FACE,{"disambiguationData":[TD([[makeQuery(id+"F11.imprint","IMPRINT",EDGE,{"derivedFrom":sQuery(id+"F11.wireOp",EDGE,"E80.0")}),1.0]])]});
            var Q3;
            Q3=makeQuery(id+"F11.imprint","IMPRINT",FACE,{"disambiguationData":[TD([[makeQuery(id+"F11.imprint","IMPRINT",EDGE,{"derivedFrom":sQuery(id+"F11.wireOp",EDGE,"E79.0")}),1.0]])]});
            var Q4;
            Q4=makeQuery(id+"F11.imprint","IMPRINT",FACE,{"disambiguationData":[TD([[makeQuery(id+"F11.imprint","IMPRINT",EDGE,{"derivedFrom":sQuery(id+"F11.wireOp",EDGE,"E81.0")}),1.0]])]});
            var Q5;
            Q5=makeQuery(id+"F11.imprint","IMPRINT",FACE,{"disambiguationData":[TD([[makeQuery(id+"F11.imprint","IMPRINT",EDGE,{"derivedFrom":sQuery(id+"F11.wireOp",EDGE,"E81.3")}),1.0]])]});
            var Q6;
            Q6=makeQuery(id+"F11.imprint","IMPRINT",FACE,{"disambiguationData":[TD([[makeQuery(id+"F11.imprint","IMPRINT",EDGE,{"derivedFrom":sQuery(id+"F11.wireOp",EDGE,"E81.4")}),1.0]])]});
            var Q7;
            Q7=makeQuery(id+"F11.imprint","IMPRINT",FACE,{"disambiguationData":[TD([[makeQuery(id+"F11.imprint","IMPRINT",EDGE,{"derivedFrom":sQuery(id+"F11.wireOp",EDGE,"E81.10")}),1.0]])]});
            var Q8;
            Q8=makeQuery(id+"F11.imprint","IMPRINT",FACE,{"disambiguationData":[TD([[makeQuery(id+"F11.imprint","IMPRINT",EDGE,{"derivedFrom":sQuery(id+"F11.wireOp",EDGE,"E81.6")}),1.0]])]});
            var Q9;
            Q9=makeQuery(id+"F11.imprint","IMPRINT",FACE,{"disambiguationData":[TD([[makeQuery(id+"F11.imprint","IMPRINT",EDGE,{"derivedFrom":sQuery(id+"F11.wireOp",EDGE,"E81.8")}),1.0]])]});
            var Q10;
            Q10=makeQuery(id+"F11.imprint","IMPRINT",FACE,{"disambiguationData":[TD([[makeQuery(id+"F11.imprint","IMPRINT",EDGE,{"derivedFrom":sQuery(id+"F11.wireOp",EDGE,"E81.12")}),1.0]])]});
            var Q11;
            Q11=makeQuery(id+"F11.imprint","IMPRINT",FACE,{"disambiguationData":[TD([[makeQuery(id+"F11.imprint","IMPRINT",EDGE,{"derivedFrom":sQuery(id+"F11.wireOp",EDGE,"E81.14")}),1.0]])]});
            extrude(context, id + "F16", {"entities" : qUnion([Q0, Q1, Q2, Q3, Q4, Q5, Q6, Q7, Q8, Q9, Q10, Q11]), "operationType" : NewBodyOperationType.ADD, "depth" : -20 * mm, "offsetDistance" : 25 * mm});
        }
        {
            var Q0;
            Q0=makeQuery(id+"F12.opExtrude","SWEPT_FACE",FACE,{"disambiguationData":[OSD([sQuery(id+"F11.wireOp",EDGE,"e2144d62-b7ac-4b5f-b738-c244b41c5520.3")])]});
            var Q1;
            Q1=makeQuery(id+"F12.opExtrude","SWEPT_FACE",FACE,{"disambiguationData":[OSD([sQuery(id+"F11.wireOp",EDGE,"E85.0")])]});
            cPlane(context, id + "F17", {"entities" : qUnion([Q0, Q1]), "cplaneType" : CPlaneType.OFFSET, "offset" : 0 * mm, "width" : 150 * mm, "height" : 150 * mm});
        }
        {
            var Q0;
            Q0=qCreatedBy(id+"F10.planeOp",FACE);
            var sketch = newSketch(context, id + "F18", { "sketchPlane" : qUnion([Q0])});
            skLineSegment(sketch, "E128.0", {"start": v(-77, -69.85) * mm, "end": v(-77, 60.75) * mm});
            skLineSegment(sketch, "E128.1", {"start": v(-77, -69.85) * mm, "end": v(2, -69.85) * mm});
            skLineSegment(sketch, "E128.2", {"start": v(2, 60.75) * mm, "end": v(2, -69.85) * mm});
            skLineSegment(sketch, "E128.3", {"start": v(-77, 60.75) * mm, "end": v(2, 60.75) * mm});
            skLineSegment(sketch, "E129.bottom", {"start": v(-60.94, -61.67) * mm, "end": v(-14.06, -61.67) * mm});
            skLineSegment(sketch, "E129.top", {"start": v(-60.94, -63.67) * mm, "end": v(-14.06, -63.67) * mm});
            skLineSegment(sketch, "E129.left", {"start": v(-60.94, -61.67) * mm, "end": v(-60.94, -63.67) * mm});
            skLineSegment(sketch, "E129.right", {"start": v(-14.06, -61.67) * mm, "end": v(-14.06, -63.67) * mm});
            skLineSegment(sketch, "E130", {"start": v(-14.06, -61.67) * mm, "end": v(2, -61.67) * mm, "construction": true});
            skLineSegment(sketch, "E131", {"start": v(-60.94, -61.67) * mm, "end": v(-77, -61.67) * mm, "construction": true});
            skLineSegment(sketch, "E132.0.1.0", {"start": v(-60.94, -53.67) * mm, "end": v(-14.06, -53.67) * mm});
            skLineSegment(sketch, "E132.0.1.1", {"start": v(-60.94, -55.67) * mm, "end": v(-14.06, -55.67) * mm});
            skLineSegment(sketch, "E132.0.1.2", {"start": v(-60.94, -53.67) * mm, "end": v(-60.94, -55.67) * mm});
            skLineSegment(sketch, "E132.0.1.3", {"start": v(-14.06, -53.67) * mm, "end": v(-14.06, -55.67) * mm});
            skLineSegment(sketch, "E132.0.2.0", {"start": v(-60.94, -45.67) * mm, "end": v(-14.06, -45.67) * mm});
            skLineSegment(sketch, "E132.0.2.1", {"start": v(-60.94, -47.67) * mm, "end": v(-14.06, -47.67) * mm});
            skLineSegment(sketch, "E132.0.2.2", {"start": v(-60.94, -45.67) * mm, "end": v(-60.94, -47.67) * mm});
            skLineSegment(sketch, "E132.0.2.3", {"start": v(-14.06, -45.67) * mm, "end": v(-14.06, -47.67) * mm});
            skLineSegment(sketch, "E132.0.3.0", {"start": v(-60.94, -37.67) * mm, "end": v(-14.06, -37.67) * mm});
            skLineSegment(sketch, "E132.0.3.1", {"start": v(-60.94, -39.67) * mm, "end": v(-14.06, -39.67) * mm});
            skLineSegment(sketch, "E132.0.3.2", {"start": v(-60.94, -37.67) * mm, "end": v(-60.94, -39.67) * mm});
            skLineSegment(sketch, "E132.0.3.3", {"start": v(-14.06, -37.67) * mm, "end": v(-14.06, -39.67) * mm});
            skLineSegment(sketch, "E132.0.4.0", {"start": v(-60.94, -29.67) * mm, "end": v(-14.06, -29.67) * mm});
            skLineSegment(sketch, "E132.0.4.1", {"start": v(-60.94, -31.67) * mm, "end": v(-14.06, -31.67) * mm});
            skLineSegment(sketch, "E132.0.4.2", {"start": v(-60.94, -29.67) * mm, "end": v(-60.94, -31.67) * mm});
            skLineSegment(sketch, "E132.0.4.3", {"start": v(-14.06, -29.67) * mm, "end": v(-14.06, -31.67) * mm});
            skLineSegment(sketch, "E132.0.5.0", {"start": v(-60.94, -21.67) * mm, "end": v(-14.06, -21.67) * mm});
            skLineSegment(sketch, "E132.0.5.1", {"start": v(-60.94, -23.67) * mm, "end": v(-14.06, -23.67) * mm});
            skLineSegment(sketch, "E132.0.5.2", {"start": v(-60.94, -21.67) * mm, "end": v(-60.94, -23.67) * mm});
            skLineSegment(sketch, "E132.0.5.3", {"start": v(-14.06, -21.67) * mm, "end": v(-14.06, -23.67) * mm});
            skLineSegment(sketch, "E132.0.6.0", {"start": v(-60.94, -13.67) * mm, "end": v(-14.06, -13.67) * mm});
            skLineSegment(sketch, "E132.0.6.1", {"start": v(-60.94, -15.67) * mm, "end": v(-14.06, -15.67) * mm});
            skLineSegment(sketch, "E132.0.6.2", {"start": v(-60.94, -13.67) * mm, "end": v(-60.94, -15.67) * mm});
            skLineSegment(sketch, "E132.0.6.3", {"start": v(-14.06, -13.67) * mm, "end": v(-14.06, -15.67) * mm});
            skLineSegment(sketch, "E132.0.7.0", {"start": v(-60.94, -5.67) * mm, "end": v(-14.06, -5.67) * mm});
            skLineSegment(sketch, "E132.0.7.1", {"start": v(-60.94, -7.67) * mm, "end": v(-14.06, -7.67) * mm});
            skLineSegment(sketch, "E132.0.7.2", {"start": v(-60.94, -5.67) * mm, "end": v(-60.94, -7.67) * mm});
            skLineSegment(sketch, "E132.0.7.3", {"start": v(-14.06, -5.67) * mm, "end": v(-14.06, -7.67) * mm});
            skLineSegment(sketch, "E132.direction1", {"start": v(-60.94, -63.67) * mm, "end": v(-35.94, -63.67) * mm, "construction": true});
            skLineSegment(sketch, "E132.direction2", {"start": v(-60.94, -63.67) * mm, "end": v(-60.94, -55.67) * mm, "construction": true});
            skLineSegment(sketch, "E133.0.1.0", {"start": v(-60.94, 2.33) * mm, "end": v(-60.94, 0.33) * mm});
            skLineSegment(sketch, "E133.0.1.1", {"start": v(-60.94, 0.33) * mm, "end": v(-14.06, 0.33) * mm});
            skLineSegment(sketch, "E133.0.1.2", {"start": v(-60.94, 2.33) * mm, "end": v(-14.06, 2.33) * mm});
            skLineSegment(sketch, "E133.0.1.3", {"start": v(-14.06, 2.33) * mm, "end": v(-14.06, 0.33) * mm});
            skLineSegment(sketch, "E133.0.2.0", {"start": v(-60.94, 10.33) * mm, "end": v(-60.94, 8.33) * mm});
            skLineSegment(sketch, "E133.0.2.1", {"start": v(-60.94, 8.33) * mm, "end": v(-14.06, 8.33) * mm});
            skLineSegment(sketch, "E133.0.2.2", {"start": v(-60.94, 10.33) * mm, "end": v(-14.06, 10.33) * mm});
            skLineSegment(sketch, "E133.0.2.3", {"start": v(-14.06, 10.33) * mm, "end": v(-14.06, 8.33) * mm});
            skLineSegment(sketch, "E133.0.3.0", {"start": v(-60.94, 18.33) * mm, "end": v(-60.94, 16.33) * mm});
            skLineSegment(sketch, "E133.0.3.1", {"start": v(-60.94, 16.33) * mm, "end": v(-14.06, 16.33) * mm});
            skLineSegment(sketch, "E133.0.3.2", {"start": v(-60.94, 18.33) * mm, "end": v(-14.06, 18.33) * mm});
            skLineSegment(sketch, "E133.0.3.3", {"start": v(-14.06, 18.33) * mm, "end": v(-14.06, 16.33) * mm});
            skLineSegment(sketch, "E133.0.4.0", {"start": v(-60.94, 26.33) * mm, "end": v(-60.94, 24.33) * mm});
            skLineSegment(sketch, "E133.0.4.1", {"start": v(-60.94, 24.33) * mm, "end": v(-14.06, 24.33) * mm});
            skLineSegment(sketch, "E133.0.4.2", {"start": v(-60.94, 26.33) * mm, "end": v(-14.06, 26.33) * mm});
            skLineSegment(sketch, "E133.0.4.3", {"start": v(-14.06, 26.33) * mm, "end": v(-14.06, 24.33) * mm});
            skLineSegment(sketch, "E133.0.5.0", {"start": v(-60.94, 34.33) * mm, "end": v(-60.94, 32.33) * mm});
            skLineSegment(sketch, "E133.0.5.1", {"start": v(-60.94, 32.33) * mm, "end": v(-14.06, 32.33) * mm});
            skLineSegment(sketch, "E133.0.5.2", {"start": v(-60.94, 34.33) * mm, "end": v(-14.06, 34.33) * mm});
            skLineSegment(sketch, "E133.0.5.3", {"start": v(-14.06, 34.33) * mm, "end": v(-14.06, 32.33) * mm});
            skLineSegment(sketch, "E133.0.6.0", {"start": v(-60.94, 42.33) * mm, "end": v(-60.94, 40.33) * mm});
            skLineSegment(sketch, "E133.0.6.1", {"start": v(-60.94, 40.33) * mm, "end": v(-14.06, 40.33) * mm});
            skLineSegment(sketch, "E133.0.6.2", {"start": v(-60.94, 42.33) * mm, "end": v(-14.06, 42.33) * mm});
            skLineSegment(sketch, "E133.0.6.3", {"start": v(-14.06, 42.33) * mm, "end": v(-14.06, 40.33) * mm});
            skLineSegment(sketch, "E133.0.7.0", {"start": v(-60.94, 50.33) * mm, "end": v(-60.94, 48.33) * mm});
            skLineSegment(sketch, "E133.0.7.1", {"start": v(-60.94, 48.33) * mm, "end": v(-14.06, 48.33) * mm});
            skLineSegment(sketch, "E133.0.7.2", {"start": v(-60.94, 50.33) * mm, "end": v(-14.06, 50.33) * mm});
            skLineSegment(sketch, "E133.0.7.3", {"start": v(-14.06, 50.33) * mm, "end": v(-14.06, 48.33) * mm});
            skLineSegment(sketch, "E133.direction1", {"start": v(-60.94, -7.67) * mm, "end": v(-35.94, -7.67) * mm, "construction": true});
            skLineSegment(sketch, "E133.direction2", {"start": v(-60.94, -7.67) * mm, "end": v(-60.94, 0.33) * mm, "construction": true});
            skSolve(sketch);
        }
        {
            var Q0;
            Q0=makeQuery(id+"F18.imprint","IMPRINT",FACE,{"disambiguationData":[TD([[makeQuery(id+"F18.imprint","IMPRINT",EDGE,{"derivedFrom":sQuery(id+"F18.wireOp",EDGE,"E133.0.7.0")}),1.0]])]});
            var Q1;
            Q1=makeQuery(id+"F18.imprint","IMPRINT",FACE,{"disambiguationData":[TD([[makeQuery(id+"F18.imprint","IMPRINT",EDGE,{"derivedFrom":sQuery(id+"F18.wireOp",EDGE,"E133.0.6.0")}),1.0]])]});
            var Q2;
            Q2=makeQuery(id+"F18.imprint","IMPRINT",FACE,{"disambiguationData":[TD([[makeQuery(id+"F18.imprint","IMPRINT",EDGE,{"derivedFrom":sQuery(id+"F18.wireOp",EDGE,"E133.0.5.0")}),1.0]])]});
            var Q3;
            Q3=makeQuery(id+"F18.imprint","IMPRINT",FACE,{"disambiguationData":[TD([[makeQuery(id+"F18.imprint","IMPRINT",EDGE,{"derivedFrom":sQuery(id+"F18.wireOp",EDGE,"E133.0.3.0")}),1.0]])]});
            var Q4;
            Q4=makeQuery(id+"F18.imprint","IMPRINT",FACE,{"disambiguationData":[TD([[makeQuery(id+"F18.imprint","IMPRINT",EDGE,{"derivedFrom":sQuery(id+"F18.wireOp",EDGE,"E133.0.2.0")}),1.0]])]});
            var Q5;
            Q5=makeQuery(id+"F18.imprint","IMPRINT",FACE,{"disambiguationData":[TD([[makeQuery(id+"F18.imprint","IMPRINT",EDGE,{"derivedFrom":sQuery(id+"F18.wireOp",EDGE,"E133.0.1.0")}),1.0]])]});
            var Q6;
            Q6=makeQuery(id+"F18.imprint","IMPRINT",FACE,{"disambiguationData":[TD([[makeQuery(id+"F18.imprint","IMPRINT",EDGE,{"derivedFrom":sQuery(id+"F18.wireOp",EDGE,"E132.0.7.0")}),-1.0]])]});
            var Q7;
            Q7=makeQuery(id+"F18.imprint","IMPRINT",FACE,{"disambiguationData":[TD([[makeQuery(id+"F18.imprint","IMPRINT",EDGE,{"derivedFrom":sQuery(id+"F18.wireOp",EDGE,"E132.0.6.0")}),-1.0]])]});
            var Q8;
            Q8=makeQuery(id+"F18.imprint","IMPRINT",FACE,{"disambiguationData":[TD([[makeQuery(id+"F18.imprint","IMPRINT",EDGE,{"derivedFrom":sQuery(id+"F18.wireOp",EDGE,"E132.0.5.0")}),-1.0]])]});
            var Q9;
            Q9=makeQuery(id+"F18.imprint","IMPRINT",FACE,{"disambiguationData":[TD([[makeQuery(id+"F18.imprint","IMPRINT",EDGE,{"derivedFrom":sQuery(id+"F18.wireOp",EDGE,"E132.0.4.0")}),-1.0]])]});
            var Q10;
            Q10=makeQuery(id+"F18.imprint","IMPRINT",FACE,{"disambiguationData":[TD([[makeQuery(id+"F18.imprint","IMPRINT",EDGE,{"derivedFrom":sQuery(id+"F18.wireOp",EDGE,"E132.0.3.0")}),-1.0]])]});
            var Q11;
            Q11=makeQuery(id+"F18.imprint","IMPRINT",FACE,{"disambiguationData":[TD([[makeQuery(id+"F18.imprint","IMPRINT",EDGE,{"derivedFrom":sQuery(id+"F18.wireOp",EDGE,"E132.0.2.0")}),-1.0]])]});
            var Q12;
            Q12=makeQuery(id+"F18.imprint","IMPRINT",FACE,{"disambiguationData":[TD([[makeQuery(id+"F18.imprint","IMPRINT",EDGE,{"derivedFrom":sQuery(id+"F18.wireOp",EDGE,"E132.0.1.0")}),-1.0]])]});
            var Q13;
            Q13=makeQuery(id+"F18.imprint","IMPRINT",FACE,{"disambiguationData":[TD([[makeQuery(id+"F18.imprint","IMPRINT",EDGE,{"derivedFrom":sQuery(id+"F18.wireOp",EDGE,"E129.bottom")}),-1.0]])]});
            extrude(context, id + "F19", {"entities" : qUnion([Q0, Q1, Q2, Q3, Q4, Q5, Q6, Q7, Q8, Q9, Q10, Q11, Q12, Q13]), "operationType" : NewBodyOperationType.REMOVE, "oppositeDirection" : true, "depth" : 2 * mm, "offsetDistance" : 25 * mm});
        }
        {
            var Q0;
            Q0=makeQuery(id+"F9.opExtrude","SWEPT_FACE",FACE,{"disambiguationData":[OSD([sQuery(id+"F0.wireOp",EDGE,"E64.0"),sQuery(id+"F0.wireOp",EDGE,"E65.left")])]});
            cPlane(context, id + "F20", {"entities" : qUnion([Q0]), "cplaneType" : CPlaneType.OFFSET, "offset" : 0 * mm, "width" : 150 * mm, "height" : 150 * mm});
        }
        {
            var Q0;
            Q0=qCreatedBy(id+"F20.planeOp",FACE);
            var sketch = newSketch(context, id + "F21", { "sketchPlane" : qUnion([Q0])});
            skLineSegment(sketch, "E134.0", {"start": v(-48.75, 5) * mm, "end": v(-58.75, 5) * mm, "construction": true});
            skLineSegment(sketch, "E135", {"start": v(-58.75, 5) * mm, "end": v(-58.75, 0) * mm, "construction": true});
            skLineSegment(sketch, "E136", {"start": v(-58.75, 0) * mm, "end": v(-48.75, 0) * mm, "construction": true});
            skLineSegment(sketch, "E137", {"start": v(-48.75, 0) * mm, "end": v(-48.75, 5) * mm, "construction": true});
            skLineSegment(sketch, "E138", {"start": v(-58.75, 2) * mm, "end": v(-48.75, 2) * mm, "construction": true});
            skLineSegment(sketch, "E139", {"start": v(-58.75, 2) * mm, "end": v(-58.75, 0) * mm});
            skLineSegment(sketch, "E140", {"start": v(-58.75, 2) * mm, "end": v(-48.75, 2) * mm});
            skLineSegment(sketch, "E141", {"start": v(-48.75, 0) * mm, "end": v(-48.75, 2) * mm});
            skLineSegment(sketch, "E142", {"start": v(-48.75, 0) * mm, "end": v(-58.75, 0) * mm});
            skLineSegment(sketch, "E143.0", {"start": v(27.4, 5) * mm, "end": v(17.4, 5) * mm});
            skLineSegment(sketch, "E144", {"start": v(17.4, 5) * mm, "end": v(17.4, 0) * mm});
            skLineSegment(sketch, "E145", {"start": v(17.4, 0) * mm, "end": v(27.4, 0) * mm, "construction": true});
            skLineSegment(sketch, "E146", {"start": v(27.4, 0) * mm, "end": v(27.4, 5) * mm});
            skLineSegment(sketch, "E147", {"start": v(17.4, 2) * mm, "end": v(27.4, 2) * mm, "construction": true});
            skLineSegment(sketch, "E148", {"start": v(17.4, 2) * mm, "end": v(17.4, 0) * mm});
            skLineSegment(sketch, "E149", {"start": v(17.4, 2) * mm, "end": v(27.4, 2) * mm});
            skLineSegment(sketch, "E150", {"start": v(27.4, 0) * mm, "end": v(27.4, 2) * mm});
            skLineSegment(sketch, "E151", {"start": v(27.4, 0) * mm, "end": v(17.4, 0) * mm});
            skSolve(sketch);
        }
        {
            var Q0;
            Q0=makeQuery(id+"Fdf0slAXkUaVCT8_2.boolean.opBoolean","COPY",EDGE,{"derivedFrom":makeQuery(id+"Fdf0slAXkUaVCT8_2.opExtrude","CAP_EDGE",EDGE,{"disambiguationData":[OSD([sQuery(id+"F21.wireOp",EDGE,"E149")])],"isStart":true})});
            var Q1;
            Q1=makeQuery(id+"Fdf0slAXkUaVCT8_2.boolean.opBoolean","COPY",EDGE,{"derivedFrom":makeQuery(id+"Fdf0slAXkUaVCT8_2.opExtrude","CAP_EDGE",EDGE,{"disambiguationData":[OSD([sQuery(id+"F21.wireOp",EDGE,"E140")])],"isStart":true})});
            var Q2;
            Q2=makeQuery(id+"F12.opExtrude","CAP_EDGE",EDGE,{"disambiguationData":[OSD([sQuery(id+"F11.wireOp",EDGE,"E86.0")])],"isStart":true});
            var Q3;
            Q3=makeQuery(id+"F12.opExtrude","CAP_EDGE",EDGE,{"disambiguationData":[OSD([sQuery(id+"F11.wireOp",EDGE,"E87.0")])],"isStart":true});
            var Q4;
            Q4=makeQuery(id+"F12.opExtrude","CAP_EDGE",EDGE,{"disambiguationData":[OSD([sQuery(id+"F11.wireOp",EDGE,"E84.0")])],"isStart":true});
            var Q5;
            Q5=makeQuery(id+"F12.opExtrude","CAP_EDGE",EDGE,{"disambiguationData":[OSD([sQuery(id+"F11.wireOp",EDGE,"E85.0")])],"isStart":true});
            var Q6;
            Q6=makeQuery(id+"F12.opExtrude","SWEPT_EDGE",EDGE,{"disambiguationData":[OSD([sQuery(id+"F11.wireOp",EDGE,"E84.0"),sQuery(id+"F11.wireOp",EDGE,"E85.0")])]});
            var Q7;
            Q7=makeQuery(id+"F12.opExtrude","SWEPT_EDGE",EDGE,{"disambiguationData":[OSD([sQuery(id+"F11.wireOp",EDGE,"E85.0"),sQuery(id+"F11.wireOp",EDGE,"E86.0")])]});
            var Q8;
            Q8=makeQuery(id+"F12.opExtrude","SWEPT_EDGE",EDGE,{"disambiguationData":[OSD([sQuery(id+"F11.wireOp",EDGE,"E86.0"),sQuery(id+"F11.wireOp",EDGE,"E87.0")])]});
            var Q9;
            Q9=makeQuery(id+"F12.opExtrude","SWEPT_EDGE",EDGE,{"disambiguationData":[OSD([sQuery(id+"F11.wireOp",EDGE,"E84.0"),sQuery(id+"F11.wireOp",EDGE,"E87.0")])]});
            var Q10;
            Q10=makeQuery(id+"F9.opExtrude","SWEPT_EDGE",EDGE,{"disambiguationData":[OSD([sQuery(id+"F0.wireOp",EDGE,"E64.0"),sQuery(id+"F0.wireOp",EDGE,"E64.3")])]});
            var Q11;
            Q11=makeQuery(id+"F9.opExtrude","SWEPT_EDGE",EDGE,{"disambiguationData":[OSD([sQuery(id+"F0.wireOp",EDGE,"E64.0"),sQuery(id+"F0.wireOp",EDGE,"E64.1")])]});
            var Q12;
            Q12=makeQuery(id+"F9.opExtrude","SWEPT_EDGE",EDGE,{"disambiguationData":[OSD([sQuery(id+"F0.wireOp",EDGE,"E64.1"),sQuery(id+"F0.wireOp",EDGE,"E64.2")])]});
            var Q13;
            Q13=makeQuery(id+"F9.opExtrude","SWEPT_EDGE",EDGE,{"disambiguationData":[OSD([sQuery(id+"F0.wireOp",EDGE,"E64.2"),sQuery(id+"F0.wireOp",EDGE,"E64.3")])]});
            chamfer(context, id + "F22", {"entities" : qUnion([Q0, Q1, Q2, Q3, Q4, Q5, Q6, Q7, Q8, Q9, Q10, Q11, Q12, Q13]), "width" : 1 * mm, "tangentPropagation" : true});
        }
        {
            var Q0;
            Q0=makeQuery(id+"F12.opExtrude","SWEPT_FACE",FACE,{"disambiguationData":[OSD([sQuery(id+"F11.wireOp",EDGE,"E87.0")])]});
            cPlane(context, id + "F23", {"entities" : qUnion([Q0]), "cplaneType" : CPlaneType.OFFSET, "offset" : 0 * mm, "width" : 150 * mm, "height" : 150 * mm});
        }
        {
            var Q0;
            Q0=makeQuery(id+"F12.opExtrude","SWEPT_FACE",FACE,{"disambiguationData":[OSD([sQuery(id+"F11.wireOp",EDGE,"E86.0")])]});
            cPlane(context, id + "F24", {"entities" : qUnion([Q0]), "cplaneType" : CPlaneType.OFFSET, "offset" : 0 * mm, "width" : 150 * mm, "height" : 150 * mm});
        }
        {
            var Q0;
            Q0=qCreatedBy(id+"F23.planeOp",FACE);
            var sketch = newSketch(context, id + "F25", { "sketchPlane" : qUnion([Q0])});
            skLineSegment(sketch, "E152.0", {"start": v(-1, 37) * mm, "end": v(-1, 16) * mm});
            skLineSegment(sketch, "E152.1", {"start": v(76, 16) * mm, "end": v(-1, 16) * mm});
            skLineSegment(sketch, "E152.2", {"start": v(76, 16) * mm, "end": v(76, 37) * mm});
            skLineSegment(sketch, "E152.3", {"start": v(76, 37) * mm, "end": v(-1, 37) * mm});
            skLineSegment(sketch, "E153", {"start": v(76, 29) * mm, "end": v(73.06, 29) * mm});
            skLineSegment(sketch, "E154", {"start": v(73.06, 29) * mm, "end": v(73.06, 16) * mm});
            skPoint(sketch, "E155.0", {"position": v(64.05, 0) * mm});
            skLineSegment(sketch, "E156", {"start": v(64.05, 0) * mm, "end": v(64.05, 29) * mm});
            skLineSegment(sketch, "E157", {"start": v(51.05, 29) * mm, "end": v(51.05, 16) * mm});
            skLineSegment(sketch, "E158", {"start": v(51.05, 29) * mm, "end": v(64.05, 29) * mm});
            skSolve(sketch);
        }
        {
            var Q0;
            {var subQ0=sQuery(id+"F25.wireOp",EDGE,"kPDcbzRQ-pQXH-1Iyz-KCbH-eIWEoIzwgVjl");Q0=makeQuery(id+"F25.imprint","IMPRINT",FACE,{"disambiguationData":[TD([[makeQuery(id+"F25.imprint","IMPRINT",EDGE,{"derivedFrom":subQ0}),-1.0]])]});}
            var Q1;
            {var subQ0=sQuery(id+"F25.wireOp",EDGE,"E157");Q1=makeQuery(id+"F25.imprint","IMPRINT",FACE,{"disambiguationData":[TD([[makeQuery(id+"F25.imprint","IMPRINT",EDGE,{"derivedFrom":subQ0}),1.0]])]});}
            extrude(context, id + "F26", {"entities" : qUnion([Q0, Q1]), "operationType" : NewBodyOperationType.REMOVE, "oppositeDirection" : true, "depth" : 2 * mm, "offsetDistance" : 25 * mm});
        }
        {
            var Q0;
            Q0=qCreatedBy(id+"F17.planeOp",FACE);
            var sketch = newSketch(context, id + "F27", { "sketchPlane" : qUnion([Q0])});
            skLineSegment(sketch, "E159.0", {"start": v(-76, 36.98) * mm, "end": v(-76, 15.98) * mm});
            skLineSegment(sketch, "E159.1", {"start": v(1, 15.98) * mm, "end": v(-76, 15.98) * mm});
            skLineSegment(sketch, "E159.2", {"start": v(1, 15.98) * mm, "end": v(1, 36.98) * mm});
            skLineSegment(sketch, "E159.3", {"start": v(1, 36.98) * mm, "end": v(-76, 36.98) * mm});
            skLineSegment(sketch, "E160", {"start": v(-73.06, 15.98) * mm, "end": v(-73.06, 25.98) * mm});
            skLineSegment(sketch, "E161", {"start": v(-73.06, 25.98) * mm, "end": v(-76, 25.98) * mm});
            skLineSegment(sketch, "E162", {"start": v(-73.06, 25.98) * mm, "end": v(-1.95, 25.98) * mm});
            skLineSegment(sketch, "E163", {"start": v(1, 25.98) * mm, "end": v(-1.95, 25.98) * mm});
            skLineSegment(sketch, "E164", {"start": v(-1.95, 25.98) * mm, "end": v(-1.95, 15.98) * mm});
            skSolve(sketch);
        }
        {
            var Q0;
            {var subQ0=sQuery(id+"F27.wireOp",EDGE,"E160");Q0=makeQuery(id+"F27.imprint","IMPRINT",FACE,{"disambiguationData":[TD([[makeQuery(id+"F27.imprint","IMPRINT",EDGE,{"derivedFrom":subQ0}),-1.0]])]});}
            extrude(context, id + "F28", {"entities" : qUnion([Q0]), "operationType" : NewBodyOperationType.REMOVE, "oppositeDirection" : true, "depth" : 2 * mm, "offsetDistance" : 25 * mm});
        }
        {
            var Q0;
            Q0=makeQuery(id+"F21.imprint","IMPRINT",FACE,{"disambiguationData":[TD([[makeQuery(id+"F21.imprint","IMPRINT",EDGE,{"derivedFrom":sQuery(id+"F21.wireOp",EDGE,"E148")}),1.0]])]});
            var Q1;
            Q1=makeQuery(id+"F21.imprint","IMPRINT",FACE,{"disambiguationData":[TD([[makeQuery(id+"F21.imprint","IMPRINT",EDGE,{"derivedFrom":sQuery(id+"F21.wireOp",EDGE,"E139")}),1.0]])]});
            extrude(context, id + "F29", {"entities" : qUnion([Q0, Q1]), "operationType" : NewBodyOperationType.REMOVE, "oppositeDirection" : true, "depth" : 3 * mm, "offsetDistance" : 25 * mm});
        }
        {
            var Q0;
            Q0=qCreatedBy(id+"F24.planeOp",FACE);
            var sketch = newSketch(context, id + "F30", { "sketchPlane" : qUnion([Q0])});
            skPoint(sketch, "E165.0", {"position": v(-17.4, 2) * mm});
            skLineSegment(sketch, "E166.0", {"start": v(-17.4, 2) * mm, "end": v(-27.4, 2) * mm});
            skLineSegment(sketch, "E167.0", {"start": v(-27.4, 0) * mm, "end": v(-27.4, 2) * mm});
            skLineSegment(sketch, "E168.0", {"start": v(-67.85, 0) * mm, "end": v(58.75, 0) * mm});
            skLineSegment(sketch, "E169.0", {"start": v(58.75, 2) * mm, "end": v(48.75, 2) * mm});
            skLineSegment(sketch, "E170.0", {"start": v(48.75, 0) * mm, "end": v(48.75, 2) * mm});
            skLineSegment(sketch, "E171.0", {"start": v(58.75, 2) * mm, "end": v(58.75, 0) * mm});
            skLineSegment(sketch, "E172.0", {"start": v(-17.4, 5) * mm, "end": v(-17.4, 0) * mm});
            skSolve(sketch);
        }
        {
            var Q0;
            {var subQ0=sQuery(id+"F30.wireOp",EDGE,"E166.0");Q0=makeQuery(id+"F30.imprint","IMPRINT",FACE,{"disambiguationData":[TD([[makeQuery(id+"F30.imprint","IMPRINT",EDGE,{"derivedFrom":subQ0}),1.0]])]});}
            var Q1;
            Q1=makeQuery(id+"F30.imprint","IMPRINT",FACE,{"disambiguationData":[TD([[makeQuery(id+"F30.imprint","IMPRINT",EDGE,{"derivedFrom":sQuery(id+"F30.wireOp",EDGE,"E169.0")}),1.0]])]});
            extrude(context, id + "F31", {"entities" : qUnion([Q0, Q1]), "operationType" : NewBodyOperationType.REMOVE, "oppositeDirection" : true, "depth" : 4.5 * mm, "offsetDistance" : 25 * mm});
        }
        {
            var Q0;
            Q0=makeQuery(id+"F15.opExtrude","SWEPT_FACE",FACE,{"disambiguationData":[OSD([sQuery(id+"F11.wireOp",EDGE,"E103.3")])]});
            cPlane(context, id + "F32", {"entities" : qUnion([Q0]), "cplaneType" : CPlaneType.OFFSET, "offset" : 0 * mm, "width" : 150 * mm, "height" : 150 * mm});
        }
        {
            var Q0;
            Q0=qCreatedBy(id+"F32.planeOp",FACE);
            var sketch = newSketch(context, id + "F33", { "sketchPlane" : qUnion([Q0])});
            skLineSegment(sketch, "E173", {"start": v(0.5, 11) * mm, "end": v(0.5, 12.8) * mm});
            skLineSegment(sketch, "E174", {"start": v(0.5, 12.8) * mm, "end": v(-0.3, 12.8) * mm});
            skLineSegment(sketch, "E175", {"start": v(-0.3, 12.8) * mm, "end": v(0.5, 11) * mm});
            skLineSegment(sketch, "E176.0", {"start": v(0.5, 11) * mm, "end": v(0.5, 36) * mm, "construction": true});
            skLineSegment(sketch, "E177.0", {"start": v(0.5, 11) * mm, "end": v(2, 11) * mm});
            skPoint(sketch, "E178.0", {"position": v(0, 5) * mm});
            skLineSegment(sketch, "E179", {"start": v(0, 5) * mm, "end": v(0, 14.14) * mm});
            skPoint(sketch, "E180.0", {"position": v(2.5, 5) * mm});
            skLineSegment(sketch, "E181", {"start": v(2.5, 5) * mm, "end": v(2.5, 14.15) * mm});
            skLineSegment(sketch, "E182", {"start": v(37.5, 0) * mm, "end": v(37.5, 37.9) * mm, "construction": true});
            skLineSegment(sketch, "E183.0", {"start": v(74.5, 11) * mm, "end": v(74.5, 36) * mm});
            skLineSegment(sketch, "E184", {"start": v(0.5, 36) * mm, "end": v(37.5, 36) * mm, "construction": true});
            skLineSegment(sketch, "E185", {"start": v(37.5, 36) * mm, "end": v(74.5, 36) * mm, "construction": true});
            skLineSegment(sketch, "E186.MirrorCS", {"start": v(75.3, 12.8) * mm, "end": v(74.5, 11) * mm});
            skLineSegment(sketch, "E187.MirrorCS", {"start": v(74.5, 12.8) * mm, "end": v(75.3, 12.8) * mm});
            skLineSegment(sketch, "E188.MirrorCS", {"start": v(74.5, 11) * mm, "end": v(74.5, 36) * mm, "construction": true});
            skLineSegment(sketch, "E189", {"start": v(74.5, 12.8) * mm, "end": v(74.5, 11) * mm, "construction": true});
            skSolve(sketch);
        }
        {
            var Q0;
            Q0=makeQuery(id+"F15.opExtrude","SWEPT_FACE",FACE,{"disambiguationData":[OSD([sQuery(id+"F11.wireOp",EDGE,"E100.0")])]});
            cPlane(context, id + "F34", {"entities" : qUnion([Q0]), "cplaneType" : CPlaneType.OFFSET, "offset" : 0 * mm, "width" : 150 * mm, "height" : 150 * mm});
        }
        {
            var Q0;
            Q0=qCreatedBy(id+"F34.planeOp",FACE);
            var sketch = newSketch(context, id + "F35", { "sketchPlane" : qUnion([Q0])});
            skLineSegment(sketch, "E190.0", {"start": v(-0.3, 12.8) * mm, "end": v(0.5, 11) * mm});
            skLineSegment(sketch, "E191.0", {"start": v(0.5, 12.8) * mm, "end": v(-0.3, 12.8) * mm});
            skLineSegment(sketch, "E192.0", {"start": v(0.5, 11) * mm, "end": v(0.5, 12.8) * mm});
            skLineSegment(sketch, "E193.0", {"start": v(75.3, 12.8) * mm, "end": v(74.5, 11) * mm});
            skLineSegment(sketch, "E194.0", {"start": v(74.5, 12.8) * mm, "end": v(75.3, 12.8) * mm});
            skLineSegment(sketch, "E195.0", {"start": v(74.5, 11) * mm, "end": v(74.5, 36) * mm});
            skSolve(sketch);
        }
        {
            var Q0;
            {var subQ0=sQuery(id+"F33.wireOp",EDGE,"E175");var subQ1=sQuery(id+"F33.wireOp",EDGE,"E174");var subQ2=makeQuery(id+"F33.imprint","INTERSECT",VERTEX,{"derivedFrom":[subQ1,subQ0]});Q0=makeQuery(id+"F33.imprint","IMPRINT",FACE,{"disambiguationData":[TD([[makeQuery(id+"F33.imprint","IMPRINT",EDGE,{"disambiguationData":[TD([[subQ2,1.0]])],"derivedFrom":subQ1}),1.0]])]});}
            var Q1;
            {var subQ0=sQuery(id+"F33.wireOp",EDGE,"E176.0");var subQ1=sQuery(id+"F33.wireOp",EDGE,"E174");var subQ2=makeQuery(id+"F33.imprint","INTERSECT",VERTEX,{"derivedFrom":[subQ1,subQ0]});Q1=makeQuery(id+"F33.imprint","IMPRINT",FACE,{"disambiguationData":[TD([[makeQuery(id+"F33.imprint","IMPRINT",EDGE,{"disambiguationData":[TD([[subQ2,-1.0]])],"derivedFrom":subQ1}),1.0]])]});}
            var Q2;
            {var subQ0=sQuery(id+"F33.wireOp",EDGE,"E186.MirrorCS");Q2=makeQuery(id+"F33.imprint","IMPRINT",FACE,{"disambiguationData":[TD([[makeQuery(id+"F33.imprint","IMPRINT",EDGE,{"derivedFrom":subQ0}),-1.0]])]});}
            var Q3;
            {var subQ0=sQuery(id+"F33.wireOp",EDGE,"E173");Q3=makeQuery(id+"F33.imprint","IMPRINT",FACE,{"disambiguationData":[TD([[makeQuery(id+"F33.imprint","IMPRINT",EDGE,{"derivedFrom":subQ0}),1.0]])]});}
            var Q4;
            Q4 = qSketchRegion(id + "F35", true);
            extrude(context, id + "F36", {"entities" : qUnion([Q0, Q1, Q2, Q3, Q4]), "operationType" : NewBodyOperationType.ADD, "oppositeDirection" : true, "depth" : 9 * mm, "offsetDistance" : 25 * mm});
        }
    });
